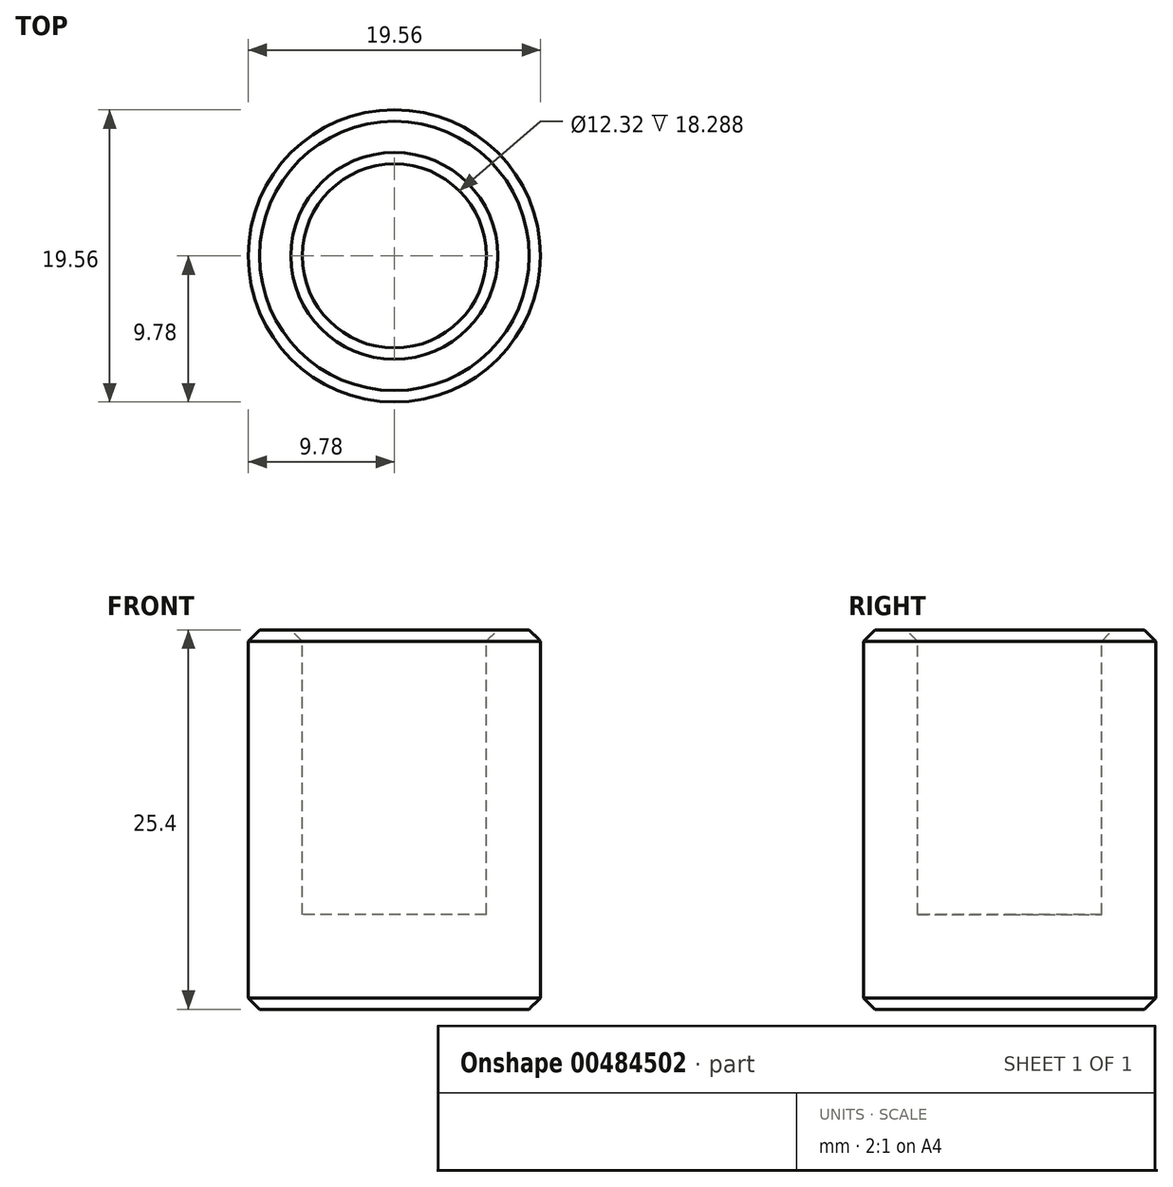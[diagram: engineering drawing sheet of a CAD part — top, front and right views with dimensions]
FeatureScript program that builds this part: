
annotation { "Feature Type Name" : "Feature", "Feature Type Description" : "" }
export const myFeature = defineFeature(function(context is Context, id is Id, definition is map)
    precondition{}
    {
        {
            var Q0;
            Q0=qCreatedBy(makeId("Top.planeOp"),FACE);
            var sketch = newSketch(context, id + "F0", { "sketchPlane" : qUnion([Q0])});
            skCircle(sketch, "E0", {"center": v(0, 0) * mm, "radius": 9.78 * mm});
            skSolve(sketch);
        }
        {
            var Q0;
            Q0 = qSketchRegion(id + "F0", true);
            extrude(context, id + "F1", {"entities" : qUnion([Q0]), "depth" : 25.4 * mm});
        }
        {
            var Q0;
            Q0=makeQuery(id+"F1.opExtrude","CAP_EDGE",EDGE,{"disambiguationData":[OSD([sQuery(id+"F0.wireOp",EDGE,"E0")])],"isStart":true});
            chamfer(context, id + "F2", {"entities" : qUnion([Q0]), "width" : 0.76 * mm, "tangentPropagation" : true});
        }
        {
            var Q0;
            Q0=makeQuery(id+"F1.opExtrude","CAP_FACE",FACE,{"disambiguationData":[OSD([sQuery(id+"F0.wireOp",EDGE,"E0")])],"isStart":false});
            var sketch = newSketch(context, id + "F3", { "sketchPlane" : qUnion([Q0])});
            skCircle(sketch, "E1", {"center": v(0, 0) * mm, "radius": 6.16 * mm});
            skSolve(sketch);
        }
        {
            var Q0;
            Q0 = qSketchRegion(id + "F3", true);
            extrude(context, id + "F4", {"entities" : qUnion([Q0]), "operationType" : NewBodyOperationType.REMOVE, "oppositeDirection" : true, "depth" : 19.05 * mm});
        }
        {
            var Q0;
            Q0=makeQuery(id+"F1.opExtrude","CAP_FACE",FACE,{"disambiguationData":[OSD([sQuery(id+"F0.wireOp",EDGE,"E0")])],"isStart":false});
            chamfer(context, id + "F5", {"entities" : qUnion([Q0]), "width" : 0.76 * mm, "tangentPropagation" : true});
        }
    });
